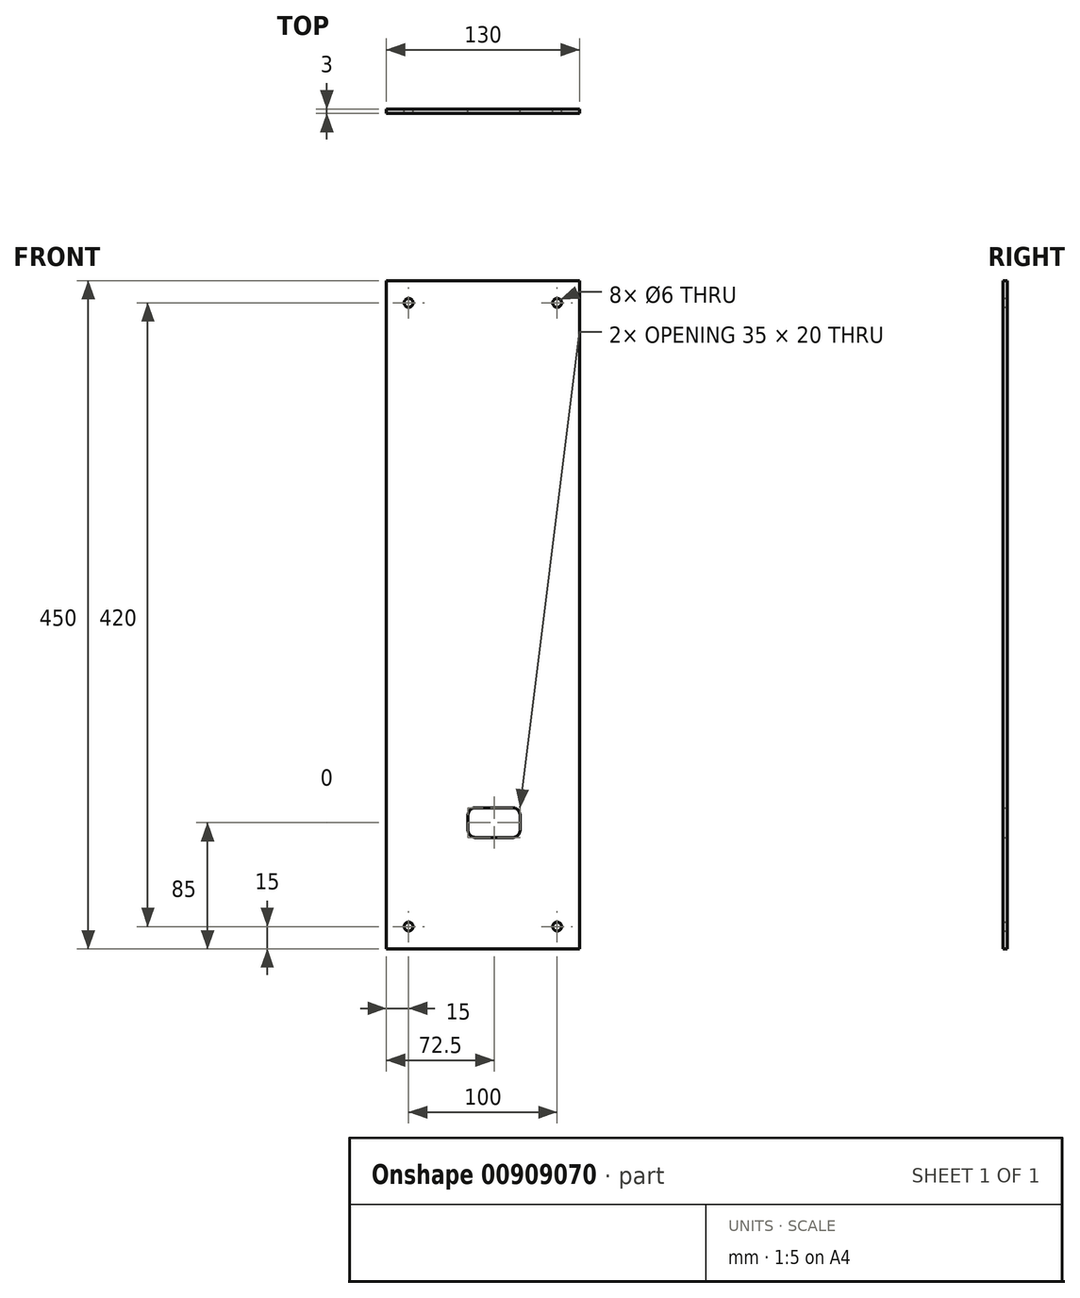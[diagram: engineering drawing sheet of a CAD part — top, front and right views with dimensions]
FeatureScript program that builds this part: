
annotation { "Feature Type Name" : "Feature", "Feature Type Description" : "" }
export const myFeature = defineFeature(function(context is Context, id is Id, definition is map)
    precondition{}
    {
        {
            var Q0;
            Q0=qCreatedBy(makeId("Front.planeOp"),FACE);
            var sketch = newSketch(context, id + "F0", { "sketchPlane" : qUnion([Q0])});
            skLineSegment(sketch, "E0.bottom", {"start": v(0, 0) * mm, "end": v(130, 0) * mm});
            skLineSegment(sketch, "E0.top", {"start": v(0, 450) * mm, "end": v(130, 450) * mm});
            skLineSegment(sketch, "E0.left", {"start": v(0, 0) * mm, "end": v(0, 450) * mm});
            skLineSegment(sketch, "E0.right", {"start": v(130, 0) * mm, "end": v(130, 450) * mm});
            skCircle(sketch, "E1", {"center": v(15, 15) * mm, "radius": 3 * mm});
            skCircle(sketch, "E2", {"center": v(115, 15) * mm, "radius": 3 * mm});
            skCircle(sketch, "E3", {"center": v(15, 435) * mm, "radius": 3 * mm});
            skCircle(sketch, "E4", {"center": v(115, 435) * mm, "radius": 3 * mm});
            skLineSegment(sketch, "E5.bottom", {"start": v(60, 95) * mm, "end": v(85, 95) * mm});
            skLineSegment(sketch, "E5.top", {"start": v(60, 75) * mm, "end": v(85, 75) * mm});
            skLineSegment(sketch, "E5.left", {"start": v(55, 90) * mm, "end": v(55, 80) * mm});
            skLineSegment(sketch, "E5.right", {"start": v(90, 90) * mm, "end": v(90, 80) * mm});
            skPoint(sketch, "E6.visualSharp", {"position": v(55, 95) * mm});
            skArc(sketch, "E6.filletArc", {"start": v(60, 95) * mm, "mid": v(56.46, 93.54) * mm, "end": v(55, 90) * mm});
            skPoint(sketch, "E7.visualSharp", {"position": v(55, 75) * mm});
            skArc(sketch, "E7.filletArc", {"start": v(55, 80) * mm, "mid": v(56.46, 76.46) * mm, "end": v(60, 75) * mm});
            skPoint(sketch, "E8.visualSharp", {"position": v(90, 75) * mm});
            skArc(sketch, "E8.filletArc", {"start": v(85, 75) * mm, "mid": v(88.54, 76.46) * mm, "end": v(90, 80) * mm});
            skPoint(sketch, "E9.visualSharp", {"position": v(90, 95) * mm});
            skArc(sketch, "E9.filletArc", {"start": v(90, 90) * mm, "mid": v(88.54, 93.54) * mm, "end": v(85, 95) * mm});
            skSolve(sketch);
        }
        {
            var Q0;
            Q0=makeQuery(id+"F0.imprint","IMPRINT",FACE,{"disambiguationData":[TD([[makeQuery(id+"F0.imprint","IMPRINT",EDGE,{"derivedFrom":sQuery(id+"F0.wireOp",EDGE,"E0.bottom")}),1.0]])]});
            extrude(context, id + "F1", {"entities" : qUnion([Q0]), "depth" : 3 * mm, "offsetDistance" : 25 * mm});
        }
    });
